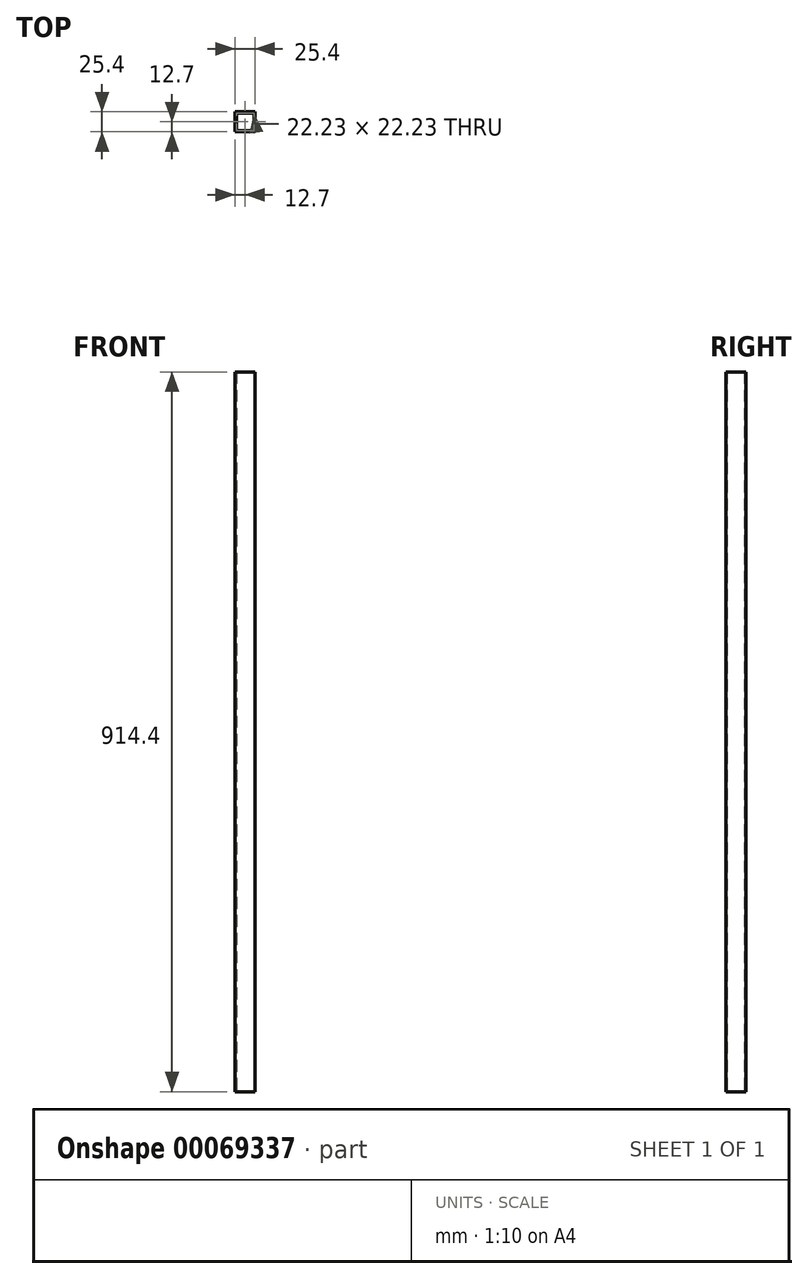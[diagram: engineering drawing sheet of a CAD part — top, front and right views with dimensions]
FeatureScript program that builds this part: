
annotation { "Feature Type Name" : "Feature", "Feature Type Description" : "" }
export const myFeature = defineFeature(function(context is Context, id is Id, definition is map)
    precondition{}
    {
        {
            var Q0;
            Q0=qCreatedBy(makeId("Top.planeOp"),FACE);
            var sketch = newSketch(context, id + "F0", { "sketchPlane" : qUnion([Q0])});
            skLineSegment(sketch, "E0.bottom", {"start": v(0, 0) * mm, "end": v(25.4, 0) * mm});
            skLineSegment(sketch, "E0.top", {"start": v(0, 25.4) * mm, "end": v(25.4, 25.4) * mm});
            skLineSegment(sketch, "E0.left", {"start": v(0, 0) * mm, "end": v(0, 25.4) * mm});
            skLineSegment(sketch, "E0.right", {"start": v(25.4, 0) * mm, "end": v(25.4, 25.4) * mm});
            skLineSegment(sketch, "E1.bottom", {"start": v(1.59, 1.59) * mm, "end": v(23.81, 1.59) * mm});
            skLineSegment(sketch, "E1.top", {"start": v(1.59, 23.81) * mm, "end": v(23.81, 23.81) * mm});
            skLineSegment(sketch, "E1.left", {"start": v(1.59, 1.59) * mm, "end": v(1.59, 23.81) * mm});
            skLineSegment(sketch, "E1.right", {"start": v(23.81, 1.59) * mm, "end": v(23.81, 23.81) * mm});
            skSolve(sketch);
        }
        {
            var Q0;
            Q0=makeQuery(id+"F0.imprint","IMPRINT",FACE,{"disambiguationData":[TD([[makeQuery(id+"F0.imprint","IMPRINT",EDGE,{"derivedFrom":sQuery(id+"F0.wireOp",EDGE,"E0.bottom")}),1.0]])]});
            extrude(context, id + "F1", {"entities" : qUnion([Q0]), "depth" : 914.4 * mm});
        }
    });
